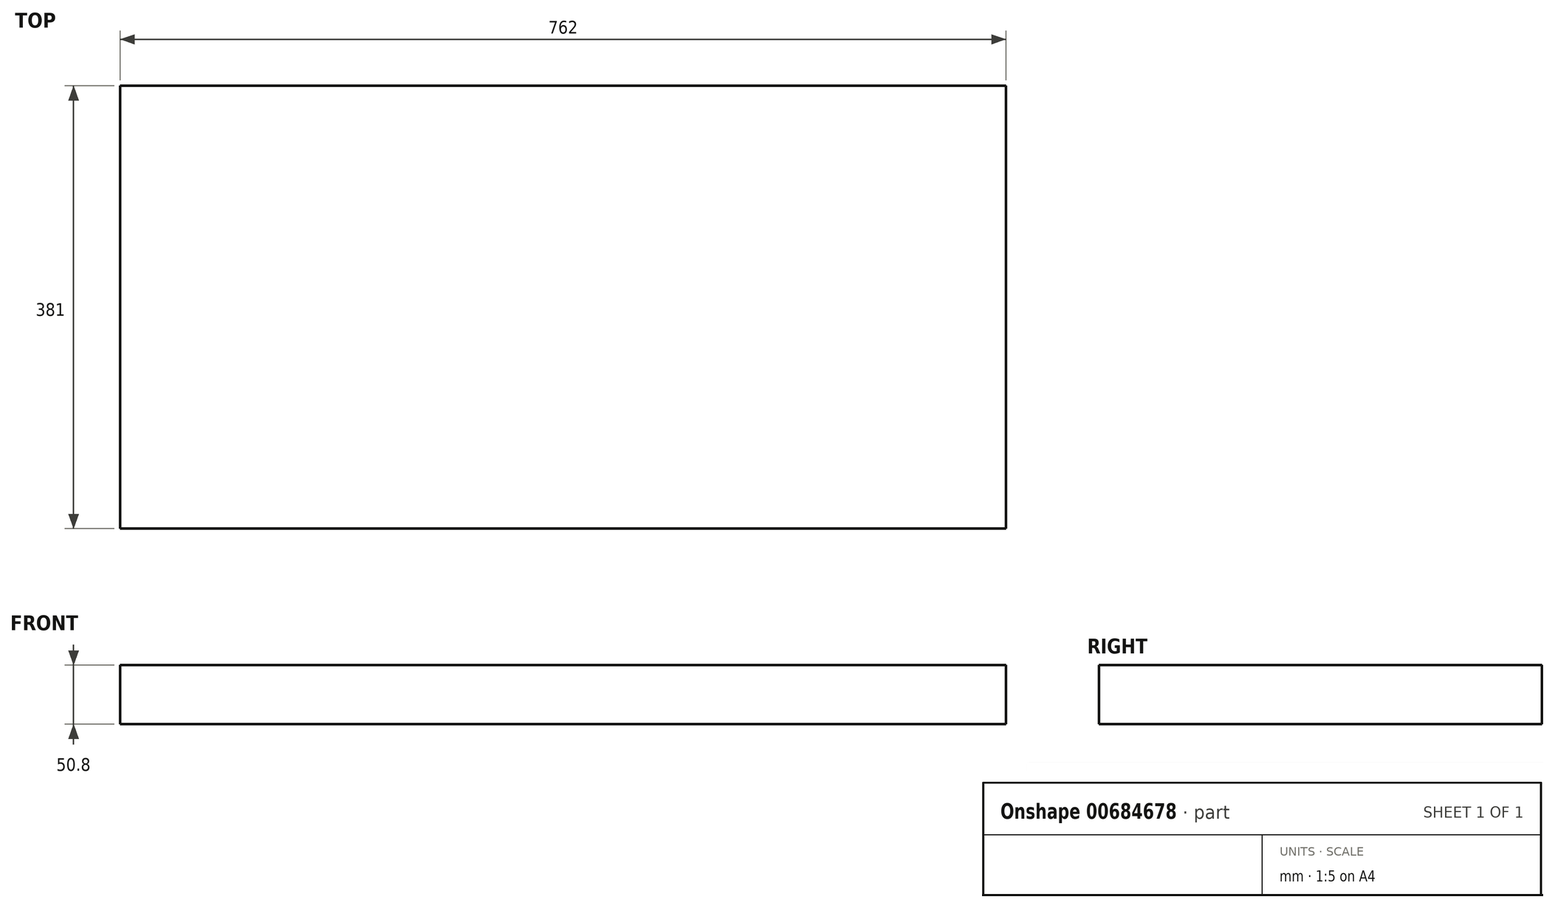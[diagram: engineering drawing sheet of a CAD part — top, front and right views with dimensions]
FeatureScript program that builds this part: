
annotation { "Feature Type Name" : "Feature", "Feature Type Description" : "" }
export const myFeature = defineFeature(function(context is Context, id is Id, definition is map)
    precondition{}
    {
        {
            var Q0;
            Q0=qCreatedBy(makeId("Top.planeOp"),FACE);
            var sketch = newSketch(context, id + "F0", { "sketchPlane" : qUnion([Q0])});
            skLineSegment(sketch, "E0.bottom", {"start": v(-383.35, -353.26) * mm, "end": v(378.65, -353.26) * mm});
            skLineSegment(sketch, "E0.top", {"start": v(-383.35, 27.74) * mm, "end": v(378.65, 27.74) * mm});
            skLineSegment(sketch, "E0.left", {"start": v(-383.35, -353.26) * mm, "end": v(-383.35, 27.74) * mm});
            skLineSegment(sketch, "E0.right", {"start": v(378.65, -353.26) * mm, "end": v(378.65, 27.74) * mm});
            skSolve(sketch);
        }
        {
            var Q0;
            Q0=qSketchRegion(id+"F0",true);
            extrude(context, id + "F1", {"entities" : qUnion([Q0]), "depth" : 50.8 * mm, "offsetDistance" : 25.4 * mm});
        }
    });
